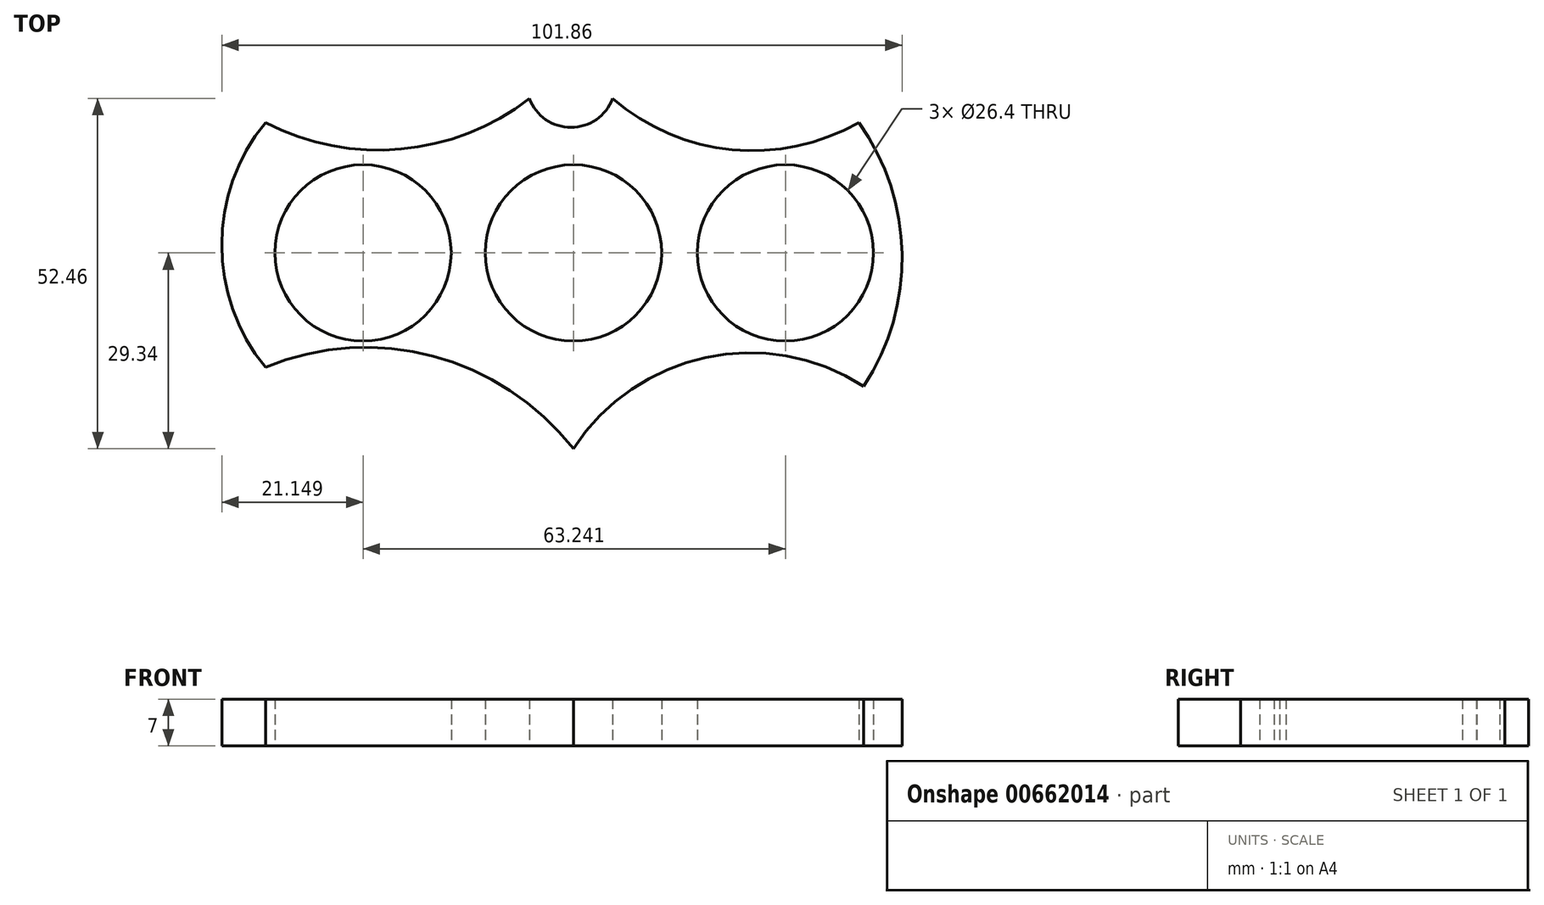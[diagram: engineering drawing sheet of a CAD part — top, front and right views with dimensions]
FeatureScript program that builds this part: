
annotation { "Feature Type Name" : "Feature", "Feature Type Description" : "" }
export const myFeature = defineFeature(function(context is Context, id is Id, definition is map)
    precondition{}
    {
        {
            var Q0;
            Q0=qCreatedBy(makeId("Top.planeOp"),FACE);
            var sketch = newSketch(context, id + "F0", { "sketchPlane" : qUnion([Q0])});
            skCircle(sketch, "E0", {"center": v(0, 0) * mm, "radius": 11.2 * mm});
            skCircle(sketch, "E1", {"center": v(0, 0) * mm, "radius": 13.2 * mm});
            skCircle(sketch, "E2", {"center": v(31.74, 0) * mm, "radius": 11.2 * mm});
            skCircle(sketch, "E3", {"center": v(31.74, 0) * mm, "radius": 13.2 * mm});
            skCircle(sketch, "E4", {"center": v(-31.5, 0) * mm, "radius": 11.2 * mm});
            skCircle(sketch, "E5", {"center": v(-31.5, 0) * mm, "radius": 13.2 * mm});
            skArc(sketch, "E6", {"start": v(43.48, -20) * mm, "mid": v(49.2, -0.13) * mm, "end": v(42.76, 19.52) * mm});
            skArc(sketch, "E7", {"start": v(5.87, 23.12) * mm, "mid": v(23.74, 15.46) * mm, "end": v(42.76, 19.52) * mm});
            skArc(sketch, "E8", {"start": v(-6.59, 23.12) * mm, "mid": v(-0.36, 18.79) * mm, "end": v(5.87, 23.12) * mm});
            skArc(sketch, "E9", {"start": v(-46.11, 19.52) * mm, "mid": v(-25.82, 15.54) * mm, "end": v(-6.59, 23.12) * mm});
            skArc(sketch, "E10", {"start": v(-46.11, 19.52) * mm, "mid": v(-52.65, 1.2) * mm, "end": v(-46.11, -17.13) * mm});
            skArc(sketch, "E11", {"start": v(0, -29.34) * mm, "mid": v(-21, -15.47) * mm, "end": v(-46.11, -17.13) * mm});
            skArc(sketch, "E12", {"start": v(43.48, -20) * mm, "mid": v(19.8, -15.67) * mm, "end": v(0, -29.34) * mm});
            skSolve(sketch);
        }
        {
            var Q0;
            Q0=makeQuery(id+"F0.imprint","IMPRINT",FACE,{"disambiguationData":[TD([[makeQuery(id+"F0.imprint","IMPRINT",EDGE,{"derivedFrom":sQuery(id+"F0.wireOp",EDGE,"E1")}),-1.0]])]});
            extrude(context, id + "F1", {"entities" : qUnion([Q0]), "depth" : 7 * mm, "offsetDistance" : 25 * mm});
        }
    });
